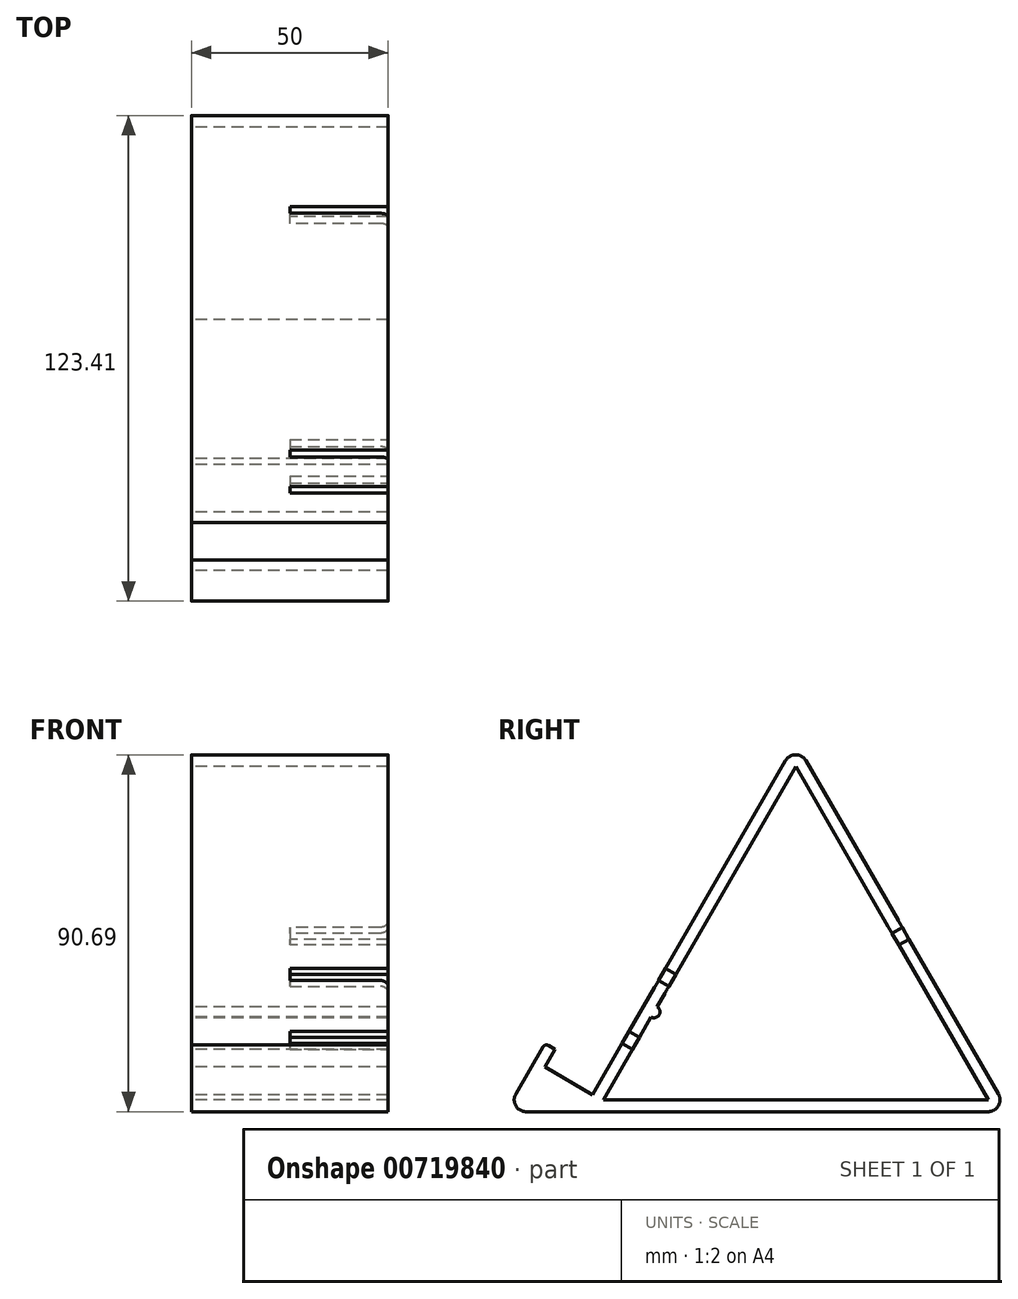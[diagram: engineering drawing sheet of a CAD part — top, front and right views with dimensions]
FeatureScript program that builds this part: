
annotation { "Feature Type Name" : "Feature", "Feature Type Description" : "" }
export const myFeature = defineFeature(function(context is Context, id is Id, definition is map)
    precondition{}
    {
        {
            var Q0;
            Q0=qCreatedBy(makeId("Right.planeOp"),FACE);
            var sketch = newSketch(context, id + "F0", { "sketchPlane" : qUnion([Q0])});
            skCircle(sketch, "E0.cCircle", {"center": v(0, 0) * mm, "radius": 31.23 * mm, "construction": true});
            skLineSegment(sketch, "E0.0", {"start": v(-54.09, -31.23) * mm, "end": v(-2.6, 57.96) * mm});
            skLineSegment(sketch, "E0.1", {"start": v(2.6, 57.96) * mm, "end": v(51.49, -26.73) * mm});
            skLineSegment(sketch, "E0.2", {"start": v(48.9, -31.23) * mm, "end": v(-54.09, -31.23) * mm});
            skPoint(sketch, "E0.0.midPoint", {"position": v(-27.04, 15.61) * mm});
            skPoint(sketch, "E1.visualSharp", {"position": v(0, 62.46) * mm});
            skArc(sketch, "E1.filletArc", {"start": v(2.6, 57.96) * mm, "mid": v(0, 59.46) * mm, "end": v(-2.6, 57.96) * mm});
            skPoint(sketch, "E2.visualSharp", {"position": v(54.09, -31.23) * mm});
            skArc(sketch, "E2.filletArc", {"start": v(48.9, -31.23) * mm, "mid": v(51.49, -29.73) * mm, "end": v(51.49, -26.73) * mm});
            skSolve(sketch);
        }
        {
            var Q0;
            Q0=makeQuery(id+"F0.imprint","IMPRINT",FACE,{"disambiguationData":[TD([[makeQuery(id+"F0.imprint","IMPRINT",EDGE,{"derivedFrom":sQuery(id+"F0.wireOp",EDGE,"E0.0")}),-1.0]])]});
            extrude(context, id + "F1", {"entities" : qUnion([Q0]), "depth" : 50 * mm, "offsetDistance" : 25 * mm});
        }
        {
            var Q0;
            Q0=makeQuery(id+"F1.opExtrude","CAP_FACE",FACE,{"disambiguationData":[OSD([sQuery(id+"F0.wireOp",EDGE,"E0.0"),sQuery(id+"F0.wireOp",EDGE,"E0.1"),sQuery(id+"F0.wireOp",EDGE,"E0.2"),sQuery(id+"F0.wireOp",EDGE,"E1.filletArc"),sQuery(id+"F0.wireOp",EDGE,"E2.filletArc")])],"isStart":false});
            var Q1;
            Q1=makeQuery(id+"F1.opExtrude","CAP_FACE",FACE,{"disambiguationData":[OSD([sQuery(id+"F0.wireOp",EDGE,"E0.0"),sQuery(id+"F0.wireOp",EDGE,"E0.1"),sQuery(id+"F0.wireOp",EDGE,"E0.2"),sQuery(id+"F0.wireOp",EDGE,"E1.filletArc"),sQuery(id+"F0.wireOp",EDGE,"E2.filletArc")])],"isStart":true});
            shell(context, id + "F2", {"entities" : qUnion([Q0, Q1]), "thickness" : 3 * mm});
        }
        {
            var Q0;
            Q0=qCreatedBy(makeId("Right.planeOp"),FACE);
            var sketch = newSketch(context, id + "F3", { "sketchPlane" : qUnion([Q0])});
            skPoint(sketch, "E3.0", {"position": v(-54.09, -31.23) * mm});
            skLineSegment(sketch, "E4.0", {"start": v(48.9, -31.23) * mm, "end": v(-54.09, -31.23) * mm});
            skLineSegment(sketch, "E5.0.0", {"start": v(-2.6, 57.96) * mm, "end": v(-54.09, -31.23) * mm});
            skLineSegment(sketch, "E5.0.2", {"start": v(-54.09, -31.23) * mm, "end": v(-2.6, 57.96) * mm});
            skLineSegment(sketch, "E6", {"start": v(-54.09, -31.23) * mm, "end": v(-68.52, -31.23) * mm});
            skLineSegment(sketch, "E7", {"start": v(-71.12, -26.73) * mm, "end": v(-64.21, -14.76) * mm});
            skLineSegment(sketch, "E8", {"start": v(-62.85, -14.4) * mm, "end": v(-61.11, -15.4) * mm});
            skLineSegment(sketch, "E9", {"start": v(-61.11, -15.4) * mm, "end": v(-63.71, -19.9) * mm});
            skLineSegment(sketch, "E10", {"start": v(-63.71, -19.9) * mm, "end": v(-51.59, -26.9) * mm});
            skPoint(sketch, "E11.visualSharp", {"position": v(-73.72, -31.23) * mm});
            skArc(sketch, "E11.filletArc", {"start": v(-71.12, -26.73) * mm, "mid": v(-71.12, -29.73) * mm, "end": v(-68.52, -31.23) * mm});
            skPoint(sketch, "E12.visualSharp", {"position": v(-63.71, -13.9) * mm});
            skArc(sketch, "E12.filletArc", {"start": v(-62.85, -14.4) * mm, "mid": v(-63.6, -14.3) * mm, "end": v(-64.21, -14.76) * mm});
            skSolve(sketch);
        }
        {
            var Q0;
            {var subQ0=sQuery(id+"F3.wireOp",EDGE,"E6");Q0=makeQuery(id+"F3.imprint","IMPRINT",FACE,{"disambiguationData":[TD([[makeQuery(id+"F3.imprint","IMPRINT",EDGE,{"derivedFrom":subQ0}),-1.0]])]});}
            extrude(context, id + "F4", {"entities" : qUnion([Q0]), "operationType" : NewBodyOperationType.ADD, "depth" : 50 * mm, "offsetDistance" : 25 * mm});
        }
        {
            var Q0;
            Q0=makeQuery(id+"F1.opExtrude","SWEPT_FACE",FACE,{"disambiguationData":[OSD([sQuery(id+"F0.wireOp",EDGE,"E0.0")])]});
            var sketch = newSketch(context, id + "F5", { "sketchPlane" : qUnion([Q0])});
            skLineSegment(sketch, "E13.bottom", {"start": v(50, -34.09) * mm, "end": v(25, -34.09) * mm});
            skLineSegment(sketch, "E13.top", {"start": v(50, -30.59) * mm, "end": v(25, -30.59) * mm});
            skLineSegment(sketch, "E13.left", {"start": v(50, -34.09) * mm, "end": v(50, -30.59) * mm});
            skLineSegment(sketch, "E13.right", {"start": v(25, -34.09) * mm, "end": v(25, -30.59) * mm});
            skSolve(sketch);
        }
        {
            var Q0;
            Q0=makeQuery(id+"F5.imprint","IMPRINT",FACE,{"disambiguationData":[TD([[makeQuery(id+"F5.imprint","IMPRINT",EDGE,{"derivedFrom":sQuery(id+"F5.wireOp",EDGE,"E13.bottom")}),-1.0]])]});
            extrude(context, id + "F6", {"entities" : qUnion([Q0]), "operationType" : NewBodyOperationType.REMOVE, "endBound" : BoundingType.UP_TO_NEXT, "oppositeDirection" : true, "depth" : 25 * mm, "offsetDistance" : 25 * mm});
        }
        {
            var Q0;
            Q0=makeQuery(id+"F1.opExtrude","SWEPT_FACE",FACE,{"disambiguationData":[OSD([sQuery(id+"F0.wireOp",EDGE,"E0.0")])]});
            var sketch = newSketch(context, id + "F7", { "sketchPlane" : qUnion([Q0])});
            skLineSegment(sketch, "E14.bottom", {"start": v(50, -15.59) * mm, "end": v(25, -15.59) * mm});
            skLineSegment(sketch, "E14.top", {"start": v(50, -12.09) * mm, "end": v(25, -12.09) * mm});
            skLineSegment(sketch, "E14.left", {"start": v(50, -15.59) * mm, "end": v(50, -12.09) * mm});
            skLineSegment(sketch, "E14.right", {"start": v(25, -15.59) * mm, "end": v(25, -12.09) * mm});
            skSolve(sketch);
        }
        {
            var Q0;
            Q0=makeQuery(id+"F7.imprint","IMPRINT",FACE,{"disambiguationData":[TD([[makeQuery(id+"F7.imprint","IMPRINT",EDGE,{"derivedFrom":sQuery(id+"F7.wireOp",EDGE,"E14.bottom")}),-1.0]])]});
            extrude(context, id + "F8", {"entities" : qUnion([Q0]), "operationType" : NewBodyOperationType.REMOVE, "endBound" : BoundingType.UP_TO_NEXT, "oppositeDirection" : true, "depth" : 25 * mm, "offsetDistance" : 25 * mm});
        }
        {
            var Q0;
            Q0=makeQuery(id+"F8.boolean.opBoolean","COPY",EDGE,{"derivedFrom":makeQuery(id+"F8.opExtrude","SWEPT_EDGE",EDGE,{"disambiguationData":[OSD([sQuery(id+"F0.wireOp",EDGE,"E0.0"),sQuery(id+"F7.wireOp",EDGE,"E14.top"),sQuery(id+"F7.wireOp",EDGE,"E14.left")])]})});
            var Q1;
            Q1=makeQuery(id+"F8.boolean.opBoolean","COPY",EDGE,{"derivedFrom":makeQuery(id+"F8.opExtrude","SWEPT_EDGE",EDGE,{"disambiguationData":[OSD([sQuery(id+"F0.wireOp",EDGE,"E0.0"),sQuery(id+"F7.wireOp",EDGE,"E14.bottom"),sQuery(id+"F7.wireOp",EDGE,"E14.left")])]})});
            var Q2;
            Q2=makeQuery(id+"F6.boolean.opBoolean","COPY",EDGE,{"derivedFrom":makeQuery(id+"F6.opExtrude","SWEPT_EDGE",EDGE,{"disambiguationData":[OSD([sQuery(id+"F0.wireOp",EDGE,"E0.0"),sQuery(id+"F5.wireOp",EDGE,"E13.top"),sQuery(id+"F5.wireOp",EDGE,"E13.left")])]})});
            var Q3;
            Q3=makeQuery(id+"F6.boolean.opBoolean","COPY",EDGE,{"derivedFrom":makeQuery(id+"F6.opExtrude","SWEPT_EDGE",EDGE,{"disambiguationData":[OSD([sQuery(id+"F0.wireOp",EDGE,"E0.0"),sQuery(id+"F5.wireOp",EDGE,"E13.bottom"),sQuery(id+"F5.wireOp",EDGE,"E13.left")])]})});
            fillet(context, id + "F9", {"entities" : qUnion([Q0, Q1, Q2, Q3]), "radius" : 2 * mm, "tangentPropagation" : true, "allowEdgeOverflow" : false});
        }
        {
            var Q0;
            Q0=qCreatedBy(makeId("Right.planeOp"),FACE);
            var sketch = newSketch(context, id + "F10", { "sketchPlane" : qUnion([Q0])});
            skCircle(sketch, "E15", {"center": v(-36, -5.88) * mm, "radius": 1.5 * mm});
            skSolve(sketch);
        }
        {
            var Q0;
            Q0=makeQuery(id+"F10.imprint","IMPRINT",FACE,{"disambiguationData":[TD([[makeQuery(id+"F10.imprint","IMPRINT",EDGE,{"derivedFrom":sQuery(id+"F10.wireOp",EDGE,"E15")}),1.0]])]});
            extrude(context, id + "F11", {"entities" : qUnion([Q0]), "operationType" : NewBodyOperationType.ADD, "depth" : 50 * mm, "offsetDistance" : 25 * mm});
        }
        {
            var Q0;
            Q0=makeQuery(id+"F1.opExtrude","SWEPT_FACE",FACE,{"disambiguationData":[OSD([sQuery(id+"F0.wireOp",EDGE,"E0.1")])]});
            var sketch = newSketch(context, id + "F12", { "sketchPlane" : qUnion([Q0])});
            skLineSegment(sketch, "E16.bottom", {"start": v(-50, 0) * mm, "end": v(-25, 0) * mm});
            skLineSegment(sketch, "E16.top", {"start": v(-50, -3.5) * mm, "end": v(-25, -3.5) * mm});
            skLineSegment(sketch, "E16.left", {"start": v(-50, 0) * mm, "end": v(-50, -3.5) * mm});
            skLineSegment(sketch, "E16.right", {"start": v(-25, 0) * mm, "end": v(-25, -3.5) * mm});
            skSolve(sketch);
        }
        {
            var Q0;
            Q0=makeQuery(id+"F12.imprint","IMPRINT",FACE,{"disambiguationData":[TD([[makeQuery(id+"F12.imprint","IMPRINT",EDGE,{"derivedFrom":sQuery(id+"F12.wireOp",EDGE,"E16.bottom")}),-1.0]])]});
            extrude(context, id + "F13", {"entities" : qUnion([Q0]), "operationType" : NewBodyOperationType.REMOVE, "oppositeDirection" : true, "depth" : 10 * mm, "offsetDistance" : 25 * mm});
        }
        {
            var Q0;
            Q0=makeQuery(id+"F13.boolean.opBoolean","COPY",EDGE,{"derivedFrom":makeQuery(id+"F13.opExtrude","SWEPT_EDGE",EDGE,{"disambiguationData":[OSD([sQuery(id+"F0.wireOp",EDGE,"E0.1"),sQuery(id+"F12.wireOp",EDGE,"sY9Y6T3m-TTTF-6fxk-MQyO-UHbyN3YBJCs7.bottom"),sQuery(id+"F12.wireOp",EDGE,"sY9Y6T3m-TTTF-6fxk-MQyO-UHbyN3YBJCs7.left")])]})});
            var Q1;
            Q1=makeQuery(id+"F13.boolean.opBoolean","COPY",EDGE,{"derivedFrom":makeQuery(id+"F13.opExtrude","SWEPT_EDGE",EDGE,{"disambiguationData":[OSD([sQuery(id+"F0.wireOp",EDGE,"E0.1"),sQuery(id+"F12.wireOp",EDGE,"sY9Y6T3m-TTTF-6fxk-MQyO-UHbyN3YBJCs7.top"),sQuery(id+"F12.wireOp",EDGE,"sY9Y6T3m-TTTF-6fxk-MQyO-UHbyN3YBJCs7.left")])]})});
            fillet(context, id + "F14", {"entities" : qUnion([Q0, Q1]), "radius" : 2 * mm, "tangentPropagation" : true, "allowEdgeOverflow" : false});
        }
    });
